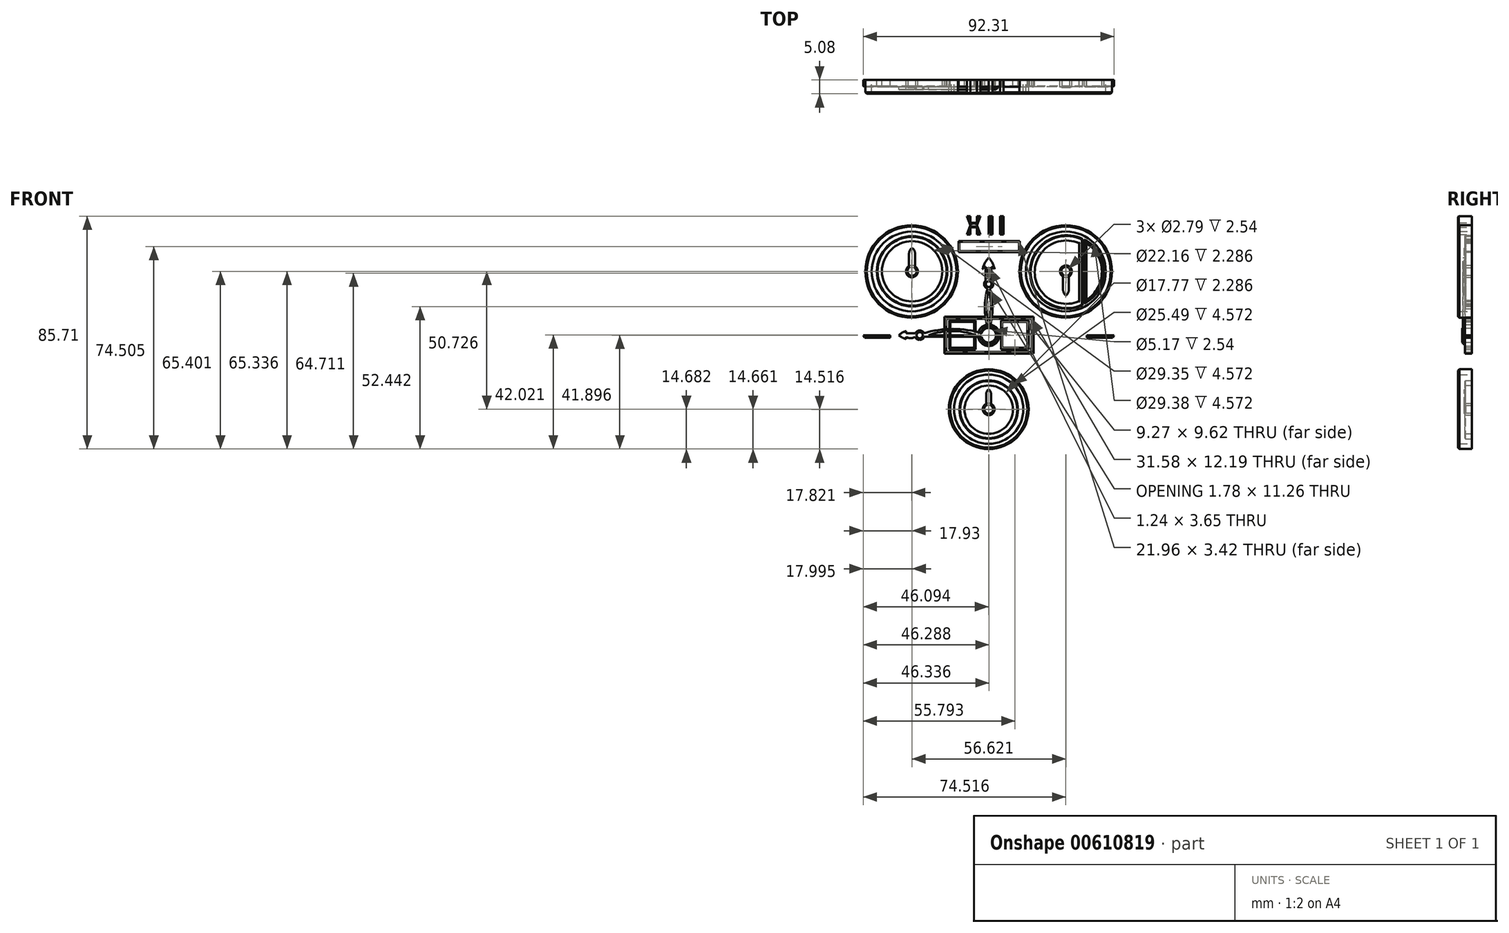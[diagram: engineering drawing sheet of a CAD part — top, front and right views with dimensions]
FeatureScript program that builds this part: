
annotation { "Feature Type Name" : "Feature", "Feature Type Description" : "" }
export const myFeature = defineFeature(function(context is Context, id is Id, definition is map)
    precondition{}
    {
        {
            var Q0;
            Q0=qCreatedBy(makeId("Front.planeOp"),FACE);
            var sketch = newSketch(context, id + "F0", { "sketchPlane" : qUnion([Q0])});
            skCircle(sketch, "E0", {"center": v(0, 0) * mm, "radius": 3.95 * mm});
            skCircle(sketch, "E1", {"center": v(0, 0) * mm, "radius": 2.59 * mm});
            skSolve(sketch);
        }
        {
            var Q0;
            Q0=qCreatedBy(makeId("Front.planeOp"),FACE);
            var sketch = newSketch(context, id + "F1", { "sketchPlane" : qUnion([Q0])});
            skCircle(sketch, "E2", {"center": v(0, -27.2) * mm, "radius": 14.68 * mm});
            skCircle(sketch, "E3", {"center": v(0, -27.2) * mm, "radius": 12.74 * mm});
            skCircle(sketch, "E4", {"center": v(-28.35, 23.46) * mm, "radius": 17 * mm});
            skCircle(sketch, "E5", {"center": v(28.35, 23.46) * mm, "radius": 17 * mm});
            skCircle(sketch, "E6", {"center": v(-28.35, 23.46) * mm, "radius": 14.68 * mm});
            skCircle(sketch, "E7", {"center": v(28.35, 23.46) * mm, "radius": 14.69 * mm});
            skLineSegment(sketch, "E8.bottom", {"start": v(0, 43.83) * mm, "end": v(1.35, 43.83) * mm});
            skLineSegment(sketch, "E8.top", {"start": v(0, 37.07) * mm, "end": v(1.35, 37.07) * mm});
            skLineSegment(sketch, "E8.left", {"start": v(0, 43.83) * mm, "end": v(0, 37.07) * mm});
            skLineSegment(sketch, "E8.right", {"start": v(1.35, 43.83) * mm, "end": v(1.35, 37.07) * mm});
            skLineSegment(sketch, "E9.bottom", {"start": v(4.12, 43.83) * mm, "end": v(5.48, 43.83) * mm});
            skLineSegment(sketch, "E9.top", {"start": v(4.12, 37.07) * mm, "end": v(5.48, 37.07) * mm});
            skLineSegment(sketch, "E9.left", {"start": v(4.12, 43.83) * mm, "end": v(4.12, 37.07) * mm});
            skLineSegment(sketch, "E9.right", {"start": v(5.48, 43.83) * mm, "end": v(5.48, 37.07) * mm});
            skLineSegment(sketch, "E10", {"start": v(-4.38, 43.83) * mm, "end": v(-3.03, 43.83) * mm});
            skLineSegment(sketch, "E11", {"start": v(-4.38, 43.83) * mm, "end": v(-4.38, 40.45) * mm});
            skPoint(sketch, "E11.endSnap0", {"position": v(0, 40.45) * mm});
            skLineSegment(sketch, "E12", {"start": v(-3.03, 43.83) * mm, "end": v(-4.38, 40.45) * mm});
            skLineSegment(sketch, "E13", {"start": v(-4.38, 40.45) * mm, "end": v(-3.03, 37.07) * mm});
            skLineSegment(sketch, "E14", {"start": v(-4.38, 40.45) * mm, "end": v(-4.38, 37.07) * mm});
            skLineSegment(sketch, "E15", {"start": v(-4.38, 37.07) * mm, "end": v(-3.03, 37.07) * mm});
            skLineSegment(sketch, "E16", {"start": v(-6.7, 43.83) * mm, "end": v(-8.05, 43.83) * mm});
            skLineSegment(sketch, "E17", {"start": v(-6.7, 43.83) * mm, "end": v(-6.7, 37.07) * mm});
            skLineSegment(sketch, "E18", {"start": v(-8.05, 43.83) * mm, "end": v(-6.7, 40.45) * mm});
            skLineSegment(sketch, "E19", {"start": v(-8.05, 37.07) * mm, "end": v(-6.7, 37.07) * mm});
            skLineSegment(sketch, "E20", {"start": v(-8.05, 37.07) * mm, "end": v(-6.7, 40.45) * mm});
            skLineSegment(sketch, "E21", {"start": v(-6.7, 39.74) * mm, "end": v(-4.38, 39.66) * mm});
            skLineSegment(sketch, "E22", {"start": v(-6.7, 41.33) * mm, "end": v(-4.38, 41.33) * mm});
            skSolve(sketch);
        }
        {
            var Q0;
            Q0=qCreatedBy(makeId("Front.planeOp"),FACE);
            var sketch = newSketch(context, id + "F2", { "sketchPlane" : qUnion([Q0])});
            skCircle(sketch, "E23", {"center": v(-28.24, 23.5) * mm, "radius": 1.4 * mm});
            skCircle(sketch, "E24", {"center": v(-28.24, 23.5) * mm, "radius": 2.18 * mm});
            skCircle(sketch, "E25", {"center": v(28.38, 23.5) * mm, "radius": 1.4 * mm});
            skCircle(sketch, "E26", {"center": v(28.38, 23.5) * mm, "radius": 2.18 * mm});
            skCircle(sketch, "E27", {"center": v(0, -27.22) * mm, "radius": 1.4 * mm});
            skCircle(sketch, "E28", {"center": v(0, -27.22) * mm, "radius": 2.17 * mm});
            skLineSegment(sketch, "E29", {"start": v(-45.64, -0.97) * mm, "end": v(-36.17, -0.97) * mm});
            skLineSegment(sketch, "E30", {"start": v(-46.17, 0) * mm, "end": v(-36.11, 0) * mm});
            skLineSegment(sketch, "E31", {"start": v(-36.24, 0) * mm, "end": v(-36.17, -0.97) * mm});
            skLineSegment(sketch, "E32", {"start": v(-46.17, 0) * mm, "end": v(-45.64, -0.97) * mm});
            skLineSegment(sketch, "E33", {"start": v(45.55, -0.97) * mm, "end": v(36.1, -0.97) * mm});
            skLineSegment(sketch, "E34", {"start": v(36.1, 0) * mm, "end": v(36.1, -0.97) * mm});
            skLineSegment(sketch, "E35", {"start": v(46.14, 0) * mm, "end": v(36.1, 0) * mm});
            skLineSegment(sketch, "E36", {"start": v(46.14, 0) * mm, "end": v(45.55, -0.97) * mm});
            skSolve(sketch);
        }
        {
            var Q0;
            Q0=qCreatedBy(makeId("Front.planeOp"),FACE);
            var sketch = newSketch(context, id + "F3", { "sketchPlane" : qUnion([Q0])});
            skLineSegment(sketch, "E37.bottom", {"start": v(-16.26, 0) * mm, "end": v(16.55, 0) * mm});
            skLineSegment(sketch, "E37.top", {"start": v(-16.26, -6.76) * mm, "end": v(16.55, -6.76) * mm});
            skLineSegment(sketch, "E37.left", {"start": v(-16.26, 0) * mm, "end": v(-16.26, -6.76) * mm});
            skLineSegment(sketch, "E37.right", {"start": v(16.55, 0) * mm, "end": v(16.55, -6.76) * mm});
            skLineSegment(sketch, "E38.top", {"start": v(-16.26, 6.76) * mm, "end": v(16.55, 6.76) * mm});
            skLineSegment(sketch, "E38.left", {"start": v(-16.26, 0) * mm, "end": v(-16.26, 6.76) * mm});
            skLineSegment(sketch, "E38.right", {"start": v(16.55, 0) * mm, "end": v(16.55, 6.76) * mm});
            skLineSegment(sketch, "E39.bottom", {"start": v(-15.67, 6.11) * mm, "end": v(15.9, 6.11) * mm});
            skLineSegment(sketch, "E39.top", {"start": v(-15.67, -6.08) * mm, "end": v(15.9, -6.08) * mm});
            skLineSegment(sketch, "E39.left", {"start": v(-15.67, 6.11) * mm, "end": v(-15.67, -6.08) * mm});
            skLineSegment(sketch, "E39.right", {"start": v(15.9, 6.11) * mm, "end": v(15.9, -6.08) * mm});
            skLineSegment(sketch, "E40", {"start": v(35.2, 35.2) * mm, "end": v(35.2, 11.64) * mm});
            skArc(sketch, "E41", {"start": v(35.2, 11.64) * mm, "mid": v(42.36, 23.42) * mm, "end": v(35.2, 35.2) * mm});
            skLineSegment(sketch, "E42.0", {"start": v(35.95, 35.2) * mm, "end": v(35.95, 34.78) * mm});
            skArc(sketch, "E43.0", {"start": v(34.84, 12.32) * mm, "mid": v(35.02, 12.41) * mm, "end": v(35.2, 12.5) * mm});
            skArc(sketch, "E44.trimOffspring", {"start": v(35.2, 34.34) * mm, "mid": v(35.02, 34.43) * mm, "end": v(34.84, 34.53) * mm});
            skArc(sketch, "E45.trimOffspring", {"start": v(35.95, 12.97) * mm, "mid": v(41.6, 23.42) * mm, "end": v(35.95, 33.88) * mm});
            skLineSegment(sketch, "E46.trimOffspring", {"start": v(35.95, 12.07) * mm, "end": v(35.95, 11.64) * mm});
            skLineSegment(sketch, "E47.trimOffspring", {"start": v(35.95, 33.88) * mm, "end": v(35.95, 12.97) * mm});
            skSolve(sketch);
        }
        {
            var Q0;
            Q0=qCreatedBy(makeId("Front.planeOp"),FACE);
            var sketch = newSketch(context, id + "F4", { "sketchPlane" : qUnion([Q0])});
            skCircle(sketch, "E48", {"center": v(0, 0) * mm, "radius": 3.17 * mm});
            skArc(sketch, "E49", {"start": v(1.07, 17.49) * mm, "mid": v(1.06, 17.52) * mm, "end": v(1.06, 17.55) * mm});
            skCircle(sketch, "E50", {"center": v(0, 18.82) * mm, "radius": 1.7 * mm});
            skCircle(sketch, "E51", {"center": v(0, 18.82) * mm, "radius": 1.05 * mm});
            skArc(sketch, "E52", {"start": v(0, 4.93) * mm, "mid": v(0.89, 10.56) * mm, "end": v(0, 16.2) * mm});
            skArc(sketch, "E53", {"start": v(0, 16.2) * mm, "mid": v(-0.89, 10.56) * mm, "end": v(0, 4.93) * mm});
            skLineSegment(sketch, "E54", {"start": v(-1.21, 20.02) * mm, "end": v(-1.21, 25.15) * mm});
            skLineSegment(sketch, "E55", {"start": v(1.06, 20.16) * mm, "end": v(1.06, 25.15) * mm});
            skArc(sketch, "E56", {"start": v(0, 25.83) * mm, "mid": v(-1.24, 25.24) * mm, "end": v(-2.26, 24.33) * mm});
            skArc(sketch, "E57", {"start": v(2.17, 24.33) * mm, "mid": v(1.11, 25.12) * mm, "end": v(0, 25.83) * mm});
            skArc(sketch, "E58", {"start": v(0, 28.57) * mm, "mid": v(-1.38, 26.59) * mm, "end": v(-2.26, 24.33) * mm});
            skArc(sketch, "E59", {"start": v(2.17, 24.33) * mm, "mid": v(1.34, 26.58) * mm, "end": v(0, 28.57) * mm});
            skLineSegment(sketch, "E60.bottom", {"start": v(-0.7, 24.66) * mm, "end": v(0.54, 24.66) * mm});
            skLineSegment(sketch, "E60.top", {"start": v(-0.7, 21) * mm, "end": v(0.54, 21) * mm});
            skLineSegment(sketch, "E60.left", {"start": v(-0.7, 24.66) * mm, "end": v(-0.7, 21) * mm});
            skLineSegment(sketch, "E60.right", {"start": v(0.54, 24.66) * mm, "end": v(0.54, 21) * mm});
            skLineSegment(sketch, "E61", {"start": v(0, 25.83) * mm, "end": v(0, 24.66) * mm});
            skLineSegment(sketch, "E62", {"start": v(0, 21) * mm, "end": v(0, 19.87) * mm});
            skLineSegment(sketch, "E63", {"start": v(0, 17.76) * mm, "end": v(0, 16.2) * mm});
            skLineSegment(sketch, "E64", {"start": v(0, 4.93) * mm, "end": v(0, 0) * mm});
            skArc(sketch, "E65.0", {"start": v(-0.98, 17.42) * mm, "mid": v(-0.98, 17.42) * mm, "end": v(-0.98, 17.42) * mm});
            skArc(sketch, "E66.0", {"start": v(0.85, 17.33) * mm, "mid": v(0.84, 17.38) * mm, "end": v(0.83, 17.42) * mm});
            skLineSegment(sketch, "E67", {"start": v(-1.21, 25.26) * mm, "end": v(-1.21, 25.15) * mm});
            skPoint(sketch, "E68.start.orphan", {"position": v(-1.21, 17.55) * mm});
            skPoint(sketch, "E69.start.orphan", {"position": v(-1.36, 25.15) * mm});
            skPoint(sketch, "E70.start.orphan", {"position": v(-1.36, 20.02) * mm});
            skArc(sketch, "E71", {"start": v(-0.41, 17.16) * mm, "mid": v(-1.42, 10.15) * mm, "end": v(-0.46, 3.14) * mm});
            skArc(sketch, "E72", {"start": v(0.4, 3.15) * mm, "mid": v(1.4, 10.15) * mm, "end": v(0.34, 17.14) * mm});
            skSolve(sketch);
        }
        {
            var Q0;
            Q0=qCreatedBy(makeId("Front.planeOp"),FACE);
            var sketch = newSketch(context, id + "F5", { "sketchPlane" : qUnion([Q0])});
            skCircle(sketch, "E73", {"center": v(-28.18, 23.52) * mm, "radius": 12.94 * mm});
            skCircle(sketch, "E74", {"center": v(-28.18, 23.52) * mm, "radius": 11.08 * mm});
            skCircle(sketch, "E75", {"center": v(0, -27.36) * mm, "radius": 10.75 * mm});
            skCircle(sketch, "E76", {"center": v(0, -27.36) * mm, "radius": 8.88 * mm});
            skLineSegment(sketch, "E77", {"start": v(34.56, 35.4) * mm, "end": v(34.56, 11.05) * mm});
            skArc(sketch, "E78", {"start": v(34.56, 35.4) * mm, "mid": v(15.15, 23.23) * mm, "end": v(34.56, 11.05) * mm});
            skLineSegment(sketch, "E79", {"start": v(33.23, 33.85) * mm, "end": v(33.23, 12.53) * mm});
            skArc(sketch, "E80", {"start": v(33.23, 33.85) * mm, "mid": v(16.91, 23.2) * mm, "end": v(33.23, 12.53) * mm});
            skSolve(sketch);
        }
        {
            var Q0;
            Q0=qCreatedBy(makeId("Front.planeOp"),FACE);
            var sketch = newSketch(context, id + "F6", { "sketchPlane" : qUnion([Q0])});
            skCircle(sketch, "E81", {"center": v(0, 0) * mm, "radius": 2.7 * mm});
            skLineSegment(sketch, "E82", {"start": v(-2.63, -0.59) * mm, "end": v(-23.73, -0.59) * mm});
            skCircle(sketch, "E83", {"center": v(-25.38, 0) * mm, "radius": 1.75 * mm});
            skCircle(sketch, "E84", {"center": v(-25.38, 0) * mm, "radius": 1.12 * mm});
            skArc(sketch, "E85", {"start": v(-30.43, -0.59) * mm, "mid": v(-28.73, -1.08) * mm, "end": v(-27.02, -0.59) * mm});
            skLineSegment(sketch, "E86", {"start": v(-26.97, 0.73) * mm, "end": v(-30.43, 0.73) * mm});
            skLineSegment(sketch, "E87", {"start": v(-30.37, 1.53) * mm, "end": v(-30.43, -1.38) * mm});
            skArc(sketch, "E88", {"start": v(-33.07, 0) * mm, "mid": v(-31.82, -0.83) * mm, "end": v(-30.43, -1.38) * mm});
            skArc(sketch, "E89", {"start": v(-30.37, 1.53) * mm, "mid": v(-31.8, 0.92) * mm, "end": v(-33.07, 0) * mm});
            skArc(sketch, "E90", {"start": v(-2.63, 0.73) * mm, "mid": v(-13.2, 2.33) * mm, "end": v(-23.78, 0.73) * mm});
            skLineSegment(sketch, "E91", {"start": v(-22.14, 0) * mm, "end": v(-4.76, 0) * mm});
            skArc(sketch, "E92", {"start": v(-4.76, 0) * mm, "mid": v(-13.45, 1.52) * mm, "end": v(-22.14, 0) * mm});
            skLineSegment(sketch, "E93", {"start": v(-23.62, 0) * mm, "end": v(-22.14, 0) * mm});
            skLineSegment(sketch, "E94", {"start": v(-30.43, 0.08) * mm, "end": v(-27.02, 0) * mm});
            skPoint(sketch, "E94.startSnap0", {"position": v(-30.4, 0.08) * mm});
            skLineSegment(sketch, "E95", {"start": v(-2.7, 0) * mm, "end": v(-4.76, 0) * mm});
            skPoint(sketch, "E95.startSnap0", {"position": v(-22.88, 0) * mm});
            skLineSegment(sketch, "E96", {"start": v(-2.63, 0.73) * mm, "end": v(-2.45, 0.73) * mm});
            skSolve(sketch);
        }
        {
            var Q0;
            Q0=qCreatedBy(makeId("Front.planeOp"),FACE);
            var sketch = newSketch(context, id + "F7", { "sketchPlane" : qUnion([Q0])});
            skLineSegment(sketch, "E97.bottom", {"start": v(4.5, 5.43) * mm, "end": v(14.76, 5.43) * mm});
            skLineSegment(sketch, "E97.top", {"start": v(4.5, -5.22) * mm, "end": v(14.76, -5.22) * mm});
            skLineSegment(sketch, "E97.left", {"start": v(4.5, 5.43) * mm, "end": v(4.5, -5.22) * mm});
            skLineSegment(sketch, "E97.right", {"start": v(14.76, 5.43) * mm, "end": v(14.76, -5.22) * mm});
            skLineSegment(sketch, "E98.bottom", {"start": v(4.99, 4.95) * mm, "end": v(14.26, 4.95) * mm});
            skLineSegment(sketch, "E98.top", {"start": v(4.99, -4.67) * mm, "end": v(14.26, -4.67) * mm});
            skLineSegment(sketch, "E98.left", {"start": v(4.99, 4.95) * mm, "end": v(4.99, -4.67) * mm});
            skLineSegment(sketch, "E98.right", {"start": v(14.26, 4.95) * mm, "end": v(14.26, -4.67) * mm});
            skLineSegment(sketch, "E99.bottom", {"start": v(-4.8, 5.43) * mm, "end": v(-14.54, 5.43) * mm});
            skLineSegment(sketch, "E99.top", {"start": v(-4.8, -5.22) * mm, "end": v(-14.54, -5.22) * mm});
            skLineSegment(sketch, "E99.left", {"start": v(-4.8, 5.43) * mm, "end": v(-4.8, -5.22) * mm});
            skLineSegment(sketch, "E99.right", {"start": v(-14.54, 5.43) * mm, "end": v(-14.54, -5.22) * mm});
            skLineSegment(sketch, "E100.bottom", {"start": v(-5.38, 4.95) * mm, "end": v(-14.08, 4.95) * mm});
            skLineSegment(sketch, "E100.top", {"start": v(-5.38, -4.67) * mm, "end": v(-14.08, -4.67) * mm});
            skLineSegment(sketch, "E100.left", {"start": v(-5.38, 4.95) * mm, "end": v(-5.38, -4.67) * mm});
            skLineSegment(sketch, "E100.right", {"start": v(-14.08, 4.95) * mm, "end": v(-14.08, -4.67) * mm});
            skLineSegment(sketch, "E101.bottom", {"start": v(-11.07, 34.66) * mm, "end": v(11.44, 34.66) * mm});
            skLineSegment(sketch, "E101.top", {"start": v(-11.07, 30.56) * mm, "end": v(11.44, 30.56) * mm});
            skLineSegment(sketch, "E101.left", {"start": v(-11.07, 34.66) * mm, "end": v(-11.07, 30.56) * mm});
            skLineSegment(sketch, "E101.right", {"start": v(11.44, 34.66) * mm, "end": v(11.44, 30.56) * mm});
            skLineSegment(sketch, "E102.bottom", {"start": v(-10.81, 30.91) * mm, "end": v(11.14, 30.91) * mm});
            skLineSegment(sketch, "E102.top", {"start": v(-10.81, 34.34) * mm, "end": v(11.14, 34.34) * mm});
            skLineSegment(sketch, "E102.left", {"start": v(-10.81, 30.91) * mm, "end": v(-10.81, 34.34) * mm});
            skLineSegment(sketch, "E102.right", {"start": v(11.14, 30.91) * mm, "end": v(11.14, 34.34) * mm});
            skSolve(sketch);
        }
        {
            var Q0;
            Q0=qCreatedBy(makeId("Front.planeOp"),FACE);
            var sketch = newSketch(context, id + "F8", { "sketchPlane" : qUnion([Q0])});
            skCircle(sketch, "E103", {"center": v(0, -27.22) * mm, "radius": 1.65 * mm});
            skLineSegment(sketch, "E104", {"start": v(-0.89, -25.82) * mm, "end": v(-0.89, -21.52) * mm});
            skLineSegment(sketch, "E105", {"start": v(0.84, -25.8) * mm, "end": v(0.84, -21.52) * mm});
            skArc(sketch, "E106", {"start": v(0, -19.94) * mm, "mid": v(-0.65, -20.62) * mm, "end": v(-0.89, -21.52) * mm});
            skArc(sketch, "E107", {"start": v(0.84, -21.52) * mm, "mid": v(0.62, -20.63) * mm, "end": v(0, -19.94) * mm});
            skCircle(sketch, "E108", {"center": v(-28.2, 23.53) * mm, "radius": 1.65 * mm});
            skLineSegment(sketch, "E109", {"start": v(-29.3, 24.77) * mm, "end": v(-29.3, 30) * mm});
            skLineSegment(sketch, "E110", {"start": v(-27.06, 24.71) * mm, "end": v(-27.06, 30) * mm});
            skArc(sketch, "E111", {"start": v(-28.2, 32.08) * mm, "mid": v(-29.01, 31.17) * mm, "end": v(-29.3, 30) * mm});
            skArc(sketch, "E112", {"start": v(-27.06, 30) * mm, "mid": v(-27.37, 31.18) * mm, "end": v(-28.2, 32.08) * mm});
            skCircle(sketch, "E113", {"center": v(28.39, 23.51) * mm, "radius": 1.65 * mm});
            skLineSegment(sketch, "E114", {"start": v(27.33, 22.25) * mm, "end": v(27.33, 16.85) * mm});
            skLineSegment(sketch, "E115", {"start": v(29.47, 22.27) * mm, "end": v(29.47, 16.85) * mm});
            skArc(sketch, "E116", {"start": v(27.33, 16.85) * mm, "mid": v(27.6, 15.63) * mm, "end": v(28.39, 14.65) * mm});
            skArc(sketch, "E117", {"start": v(28.39, 14.65) * mm, "mid": v(29.19, 15.62) * mm, "end": v(29.47, 16.85) * mm});
            skSolve(sketch);
        }
        {
            var Q0;
            Q0 = qSketchRegion(id + "F0", true);
            extrude(context, id + "F9", {"entities" : qUnion([Q0]), "depth" : 2.54 * mm, "offsetDistance" : 25.4 * mm});
        }
        {
            var Q0;
            Q0 = qSketchRegion(id + "F1", true);
            extrude(context, id + "F10", {"entities" : qUnion([Q0]), "depth" : 5.08 * mm, "offsetDistance" : 25.4 * mm});
        }
        {
            var Q0;
            Q0 = qSketchRegion(id + "F2", true);
            extrude(context, id + "F11", {"entities" : qUnion([Q0]), "depth" : 2.54 * mm, "offsetDistance" : 25.4 * mm});
        }
        {
            var Q0;
            Q0 = qSketchRegion(id + "F3", true);
            extrude(context, id + "F12", {"entities" : qUnion([Q0]), "depth" : 2.54 * mm, "offsetDistance" : 25.4 * mm});
        }
        {
            var Q0;
            Q0 = qSketchRegion(id + "F4", true);
            extrude(context, id + "F13", {"entities" : qUnion([Q0]), "depth" : 3.3 * mm, "offsetDistance" : 25.4 * mm, "hasSecondDirection" : true, "secondDirectionOppositeDirection" : false, "secondDirectionDepth" : 2.54 * mm});
        }
        {
            var Q0;
            Q0 = qSketchRegion(id + "F5", true);
            extrude(context, id + "F14", {"entities" : qUnion([Q0]), "depth" : 2.54 * mm, "offsetDistance" : 25.4 * mm});
        }
        {
            var Q0;
            Q0 = qSketchRegion(id + "F6", true);
            extrude(context, id + "F15", {"entities" : qUnion([Q0]), "depth" : 3.56 * mm, "offsetDistance" : 25.4 * mm, "hasSecondDirection" : true, "secondDirectionOppositeDirection" : false, "secondDirectionDepth" : 2.54 * mm});
        }
        {
            var Q0;
            Q0 = qSketchRegion(id + "F7", true);
            extrude(context, id + "F16", {"entities" : qUnion([Q0]), "operationType" : NewBodyOperationType.ADD, "depth" : 2.54 * mm, "offsetDistance" : 25.4 * mm});
        }
        {
            var Q0;
            Q0 = qSketchRegion(id + "F8", true);
            extrude(context, id + "F17", {"entities" : qUnion([Q0]), "depth" : 2.8 * mm, "offsetDistance" : 25.4 * mm, "hasSecondDirection" : true, "secondDirectionOppositeDirection" : false, "secondDirectionDepth" : 2.3 * mm});
        }
        {
            var Q0;
            Q0=makeQuery(id+"F10.opExtrude","CAP_EDGE",EDGE,{"disambiguationData":[OSD([sQuery(id+"F1.wireOp",EDGE,"E4")])],"isStart":false});
            var Q1;
            Q1=makeQuery(id+"F10.opExtrude","CAP_EDGE",EDGE,{"disambiguationData":[OSD([sQuery(id+"F1.wireOp",EDGE,"E5")])],"isStart":false});
            var Q2;
            Q2=makeQuery(id+"F10.opExtrude","CAP_EDGE",EDGE,{"disambiguationData":[OSD([sQuery(id+"F1.wireOp",EDGE,"E2")])],"isStart":false});
            chamfer(context, id + "F18", {"entities" : qUnion([Q0, Q1, Q2]), "width" : 0.5 * mm, "tangentPropagation" : true});
        }
        {
            var Q0;
            Q0=makeQuery(id+"F10.opExtrude","CAP_EDGE",EDGE,{"disambiguationData":[OSD([sQuery(id+"F1.wireOp",EDGE,"E6")])],"isStart":false});
            var Q1;
            Q1=makeQuery(id+"F10.opExtrude","CAP_EDGE",EDGE,{"disambiguationData":[OSD([sQuery(id+"F1.wireOp",EDGE,"E7")])],"isStart":false});
            var Q2;
            Q2=makeQuery(id+"F10.opExtrude","CAP_EDGE",EDGE,{"disambiguationData":[OSD([sQuery(id+"F1.wireOp",EDGE,"E3")])],"isStart":false});
            fillet(context, id + "F19", {"entities" : qUnion([Q0, Q1, Q2]), "radius" : 0.5 * mm, "tangentPropagation" : true, "allowEdgeOverflow" : false});
        }
        {
            var Q0;
            Q0=makeQuery(id+"F14.opExtrude","CAP_EDGE",EDGE,{"disambiguationData":[OSD([sQuery(id+"F5.wireOp",EDGE,"E73")])],"isStart":false});
            var Q1;
            Q1=makeQuery(id+"F14.opExtrude","CAP_EDGE",EDGE,{"disambiguationData":[OSD([sQuery(id+"F5.wireOp",EDGE,"E78")])],"isStart":false});
            var Q2;
            Q2=makeQuery(id+"F14.opExtrude","CAP_EDGE",EDGE,{"disambiguationData":[OSD([sQuery(id+"F5.wireOp",EDGE,"E77")])],"isStart":false});
            var Q3;
            Q3=makeQuery(id+"F12.opExtrude","CAP_EDGE",EDGE,{"disambiguationData":[OSD([sQuery(id+"F3.wireOp",EDGE,"E41")])],"isStart":false});
            var Q4;
            Q4=makeQuery(id+"F12.opExtrude","CAP_EDGE",EDGE,{"disambiguationData":[OSD([sQuery(id+"F3.wireOp",EDGE,"E40")])],"isStart":false});
            var Q5;
            Q5=makeQuery(id+"F14.opExtrude","CAP_EDGE",EDGE,{"disambiguationData":[OSD([sQuery(id+"F5.wireOp",EDGE,"E75")])],"isStart":false});
            chamfer(context, id + "F20", {"entities" : qUnion([Q0, Q1, Q2, Q3, Q4, Q5]), "width" : 0.25 * mm, "tangentPropagation" : true});
        }
        {
            var Q0;
            Q0=makeQuery(id+"F14.opExtrude","CAP_EDGE",EDGE,{"disambiguationData":[OSD([sQuery(id+"F5.wireOp",EDGE,"E74")])],"isStart":false});
            var Q1;
            Q1=makeQuery(id+"F14.opExtrude","CAP_EDGE",EDGE,{"disambiguationData":[OSD([sQuery(id+"F5.wireOp",EDGE,"E80")])],"isStart":false});
            var Q2;
            Q2=makeQuery(id+"F14.opExtrude","CAP_EDGE",EDGE,{"disambiguationData":[OSD([sQuery(id+"F5.wireOp",EDGE,"E79")])],"isStart":false});
            var Q3;
            Q3=makeQuery(id+"F14.opExtrude","CAP_EDGE",EDGE,{"disambiguationData":[OSD([sQuery(id+"F5.wireOp",EDGE,"E76")])],"isStart":false});
            var Q4;
            Q4=makeQuery(id+"F12.opExtrude","CAP_EDGE",EDGE,{"disambiguationData":[OSD([sQuery(id+"F3.wireOp",EDGE,"E45.trimOffspring")])],"isStart":false});
            var Q5;
            Q5=makeQuery(id+"F12.opExtrude","CAP_EDGE",EDGE,{"disambiguationData":[OSD([sQuery(id+"F3.wireOp",EDGE,"E47.trimOffspring")])],"isStart":false});
            fillet(context, id + "F21", {"entities" : qUnion([Q0, Q1, Q2, Q3, Q4, Q5]), "radius" : 0.25 * mm, "tangentPropagation" : true, "allowEdgeOverflow" : false});
        }
        {
            var Q0;
            Q0=makeQuery(id+"F10.opExtrude","CAP_EDGE",EDGE,{"disambiguationData":[OSD([sQuery(id+"F1.wireOp",EDGE,"E9.right")])],"isStart":false});
            var Q1;
            Q1=makeQuery(id+"F10.opExtrude","CAP_FACE",FACE,{"disambiguationData":[OSD([sQuery(id+"F1.wireOp",EDGE,"E9.bottom"),sQuery(id+"F1.wireOp",EDGE,"E9.top"),sQuery(id+"F1.wireOp",EDGE,"E9.left"),sQuery(id+"F1.wireOp",EDGE,"E9.right")])],"isStart":false});
            var Q2;
            Q2=makeQuery(id+"F10.opExtrude","CAP_FACE",FACE,{"disambiguationData":[OSD([sQuery(id+"F1.wireOp",EDGE,"E8.bottom"),sQuery(id+"F1.wireOp",EDGE,"E8.top"),sQuery(id+"F1.wireOp",EDGE,"E8.left"),sQuery(id+"F1.wireOp",EDGE,"E8.right")])],"isStart":false});
            var Q3;
            Q3=makeQuery(id+"F10.opExtrude","CAP_FACE",FACE,{"disambiguationData":[OSD([sQuery(id+"F1.wireOp",EDGE,"E10"),sQuery(id+"F1.wireOp",EDGE,"E11"),sQuery(id+"F1.wireOp",EDGE,"E12"),sQuery(id+"F1.wireOp",EDGE,"E13"),sQuery(id+"F1.wireOp",EDGE,"E14"),sQuery(id+"F1.wireOp",EDGE,"E15"),sQuery(id+"F1.wireOp",EDGE,"E16"),sQuery(id+"F1.wireOp",EDGE,"E17"),sQuery(id+"F1.wireOp",EDGE,"E18"),sQuery(id+"F1.wireOp",EDGE,"E19"),sQuery(id+"F1.wireOp",EDGE,"E20"),sQuery(id+"F1.wireOp",EDGE,"E21"),sQuery(id+"F1.wireOp",EDGE,"E22")])],"isStart":false});
            var Q4;
            Q4=makeQuery(id+"F11.opExtrude","CAP_FACE",FACE,{"disambiguationData":[OSD([sQuery(id+"F2.wireOp",EDGE,"E29"),sQuery(id+"F2.wireOp",EDGE,"E30"),sQuery(id+"F2.wireOp",EDGE,"E31"),sQuery(id+"F2.wireOp",EDGE,"E32")])],"isStart":false});
            var Q5;
            Q5=makeQuery(id+"F11.opExtrude","CAP_FACE",FACE,{"disambiguationData":[OSD([sQuery(id+"F2.wireOp",EDGE,"E33"),sQuery(id+"F2.wireOp",EDGE,"E34"),sQuery(id+"F2.wireOp",EDGE,"E35"),sQuery(id+"F2.wireOp",EDGE,"E36")])],"isStart":false});
            chamfer(context, id + "F22", {"entities" : qUnion([Q0, Q1, Q2, Q3, Q4, Q5]), "width" : 0.25 * mm, "tangentPropagation" : true});
        }
    });
